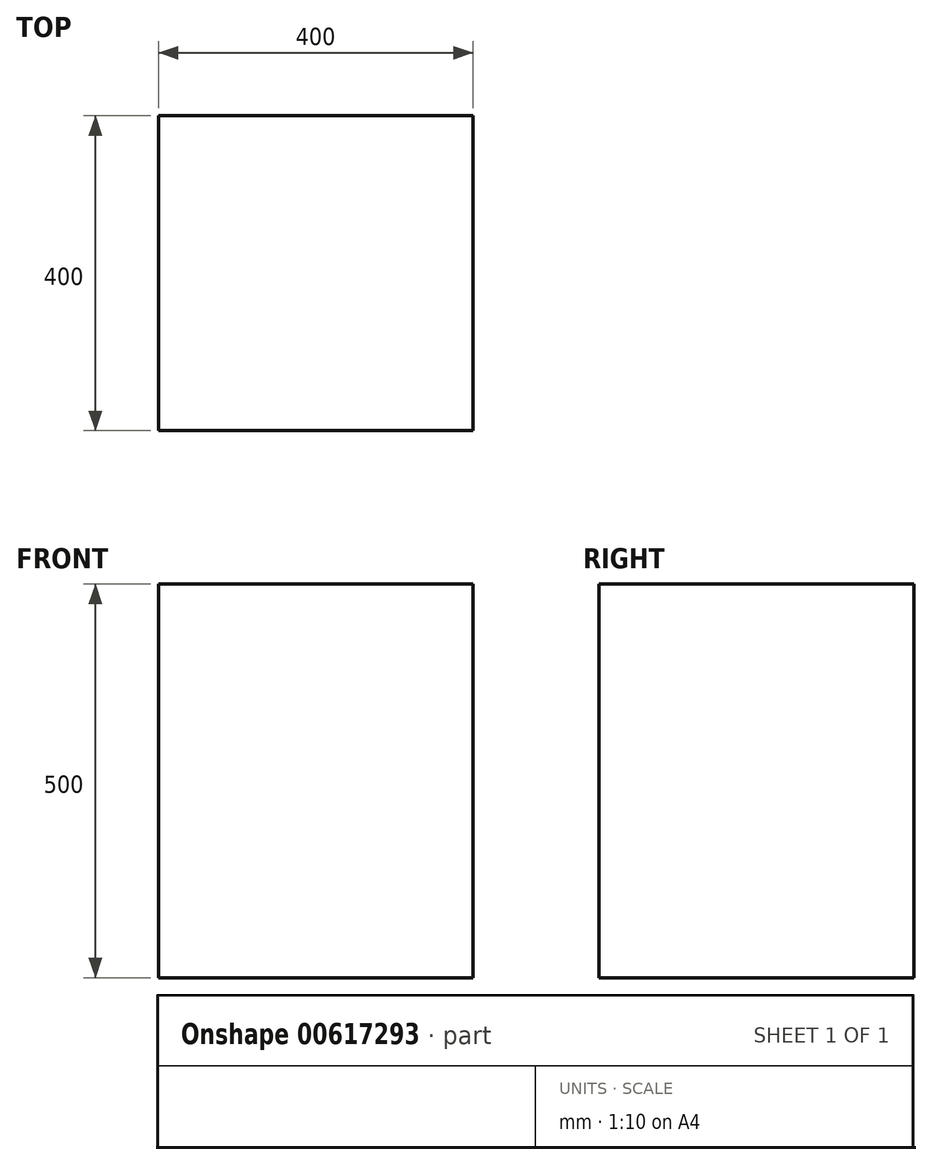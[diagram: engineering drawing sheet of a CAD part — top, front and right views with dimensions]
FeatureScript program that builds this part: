
annotation { "Feature Type Name" : "Feature", "Feature Type Description" : "" }
export const myFeature = defineFeature(function(context is Context, id is Id, definition is map)
    precondition{}
    {
        {
            var Q0;
            Q0=qCreatedBy(makeId("Top.planeOp"),FACE);
            var sketch = newSketch(context, id + "F0", { "sketchPlane" : qUnion([Q0])});
            skLineSegment(sketch, "E0.bottom", {"start": v(-207.25, 256.24) * mm, "end": v(192.75, 256.24) * mm});
            skLineSegment(sketch, "E0.top", {"start": v(-207.25, -143.76) * mm, "end": v(192.75, -143.76) * mm});
            skLineSegment(sketch, "E0.left", {"start": v(-207.25, 256.24) * mm, "end": v(-207.25, -143.76) * mm});
            skLineSegment(sketch, "E0.right", {"start": v(192.75, 256.24) * mm, "end": v(192.75, -143.76) * mm});
            skSolve(sketch);
        }
        {
            var Q0;
            Q0 = qSketchRegion(id + "F0", true);
            extrude(context, id + "F1", {"entities" : qUnion([Q0]), "depth" : 500 * mm, "offsetDistance" : 25 * mm});
        }
    });
